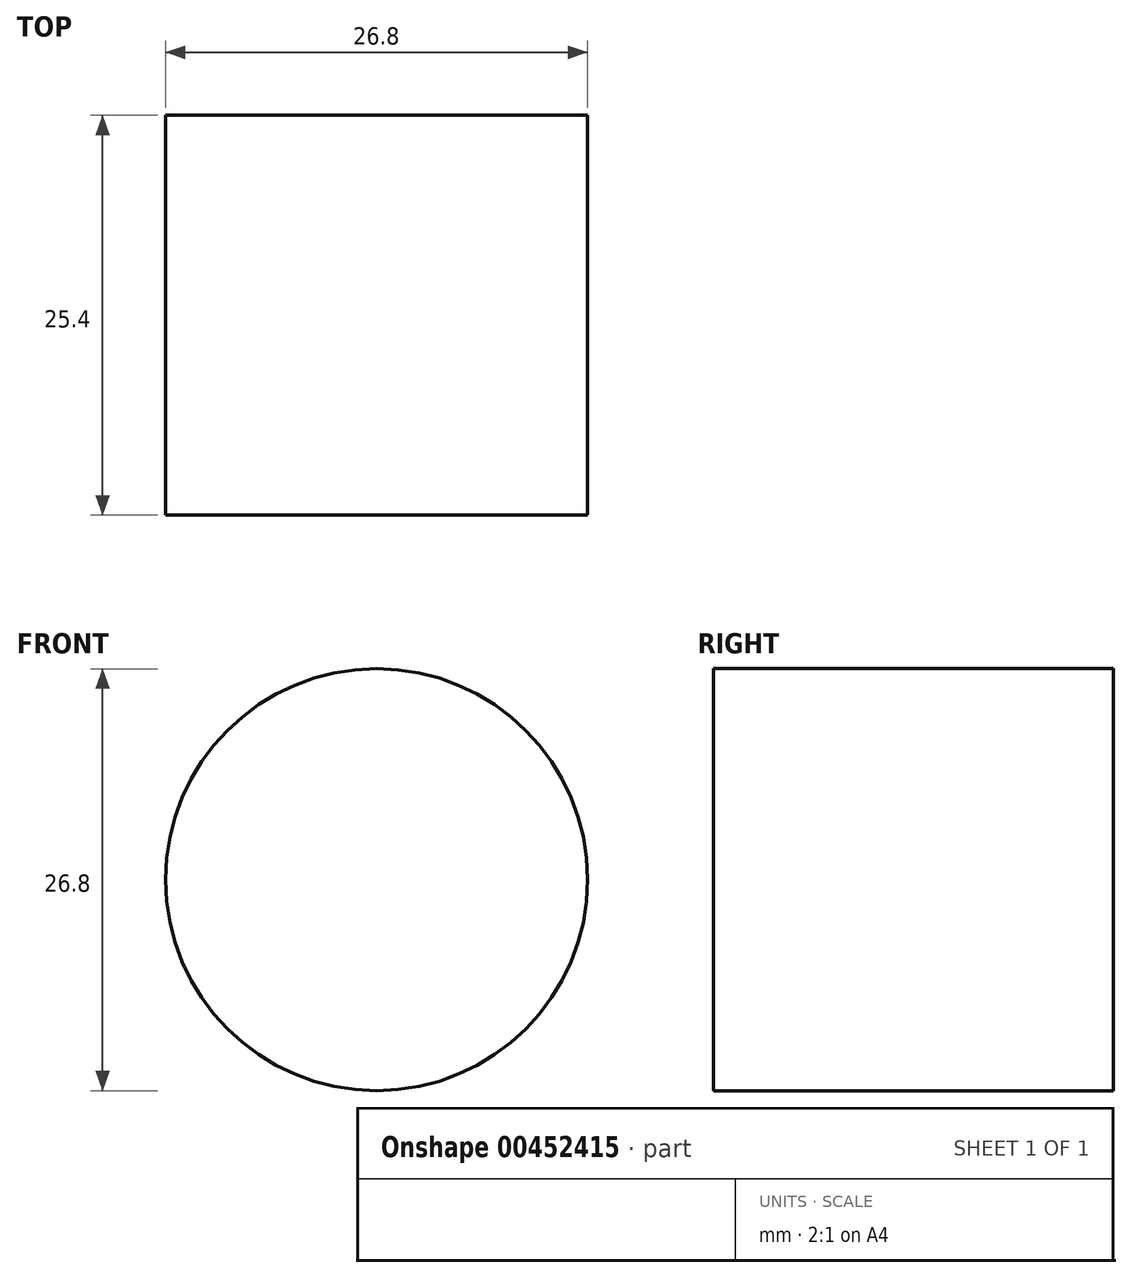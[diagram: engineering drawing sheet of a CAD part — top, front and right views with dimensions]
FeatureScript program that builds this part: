
annotation { "Feature Type Name" : "Feature", "Feature Type Description" : "" }
export const myFeature = defineFeature(function(context is Context, id is Id, definition is map)
    precondition{}
    {
        {
            var Q0;
            Q0=qCreatedBy(makeId("Front.planeOp"),FACE);
            var sketch = newSketch(context, id + "F0", { "sketchPlane" : qUnion([Q0])});
            skCircle(sketch, "E0", {"center": v(-8.5, 5.12) * mm, "radius": 13.4 * mm});
            skSolve(sketch);
        }
        {
            var Q0;
            Q0=makeQuery(id+"F0.imprint","IMPRINT",FACE,{"disambiguationData":[TD([[makeQuery(id+"F0.imprint","IMPRINT",EDGE,{"derivedFrom":sQuery(id+"F0.wireOp",EDGE,"E0")}),1.0]])]});
            extrude(context, id + "F1", {"entities" : qUnion([Q0]), "depth" : 25.4 * mm});
        }
    });
